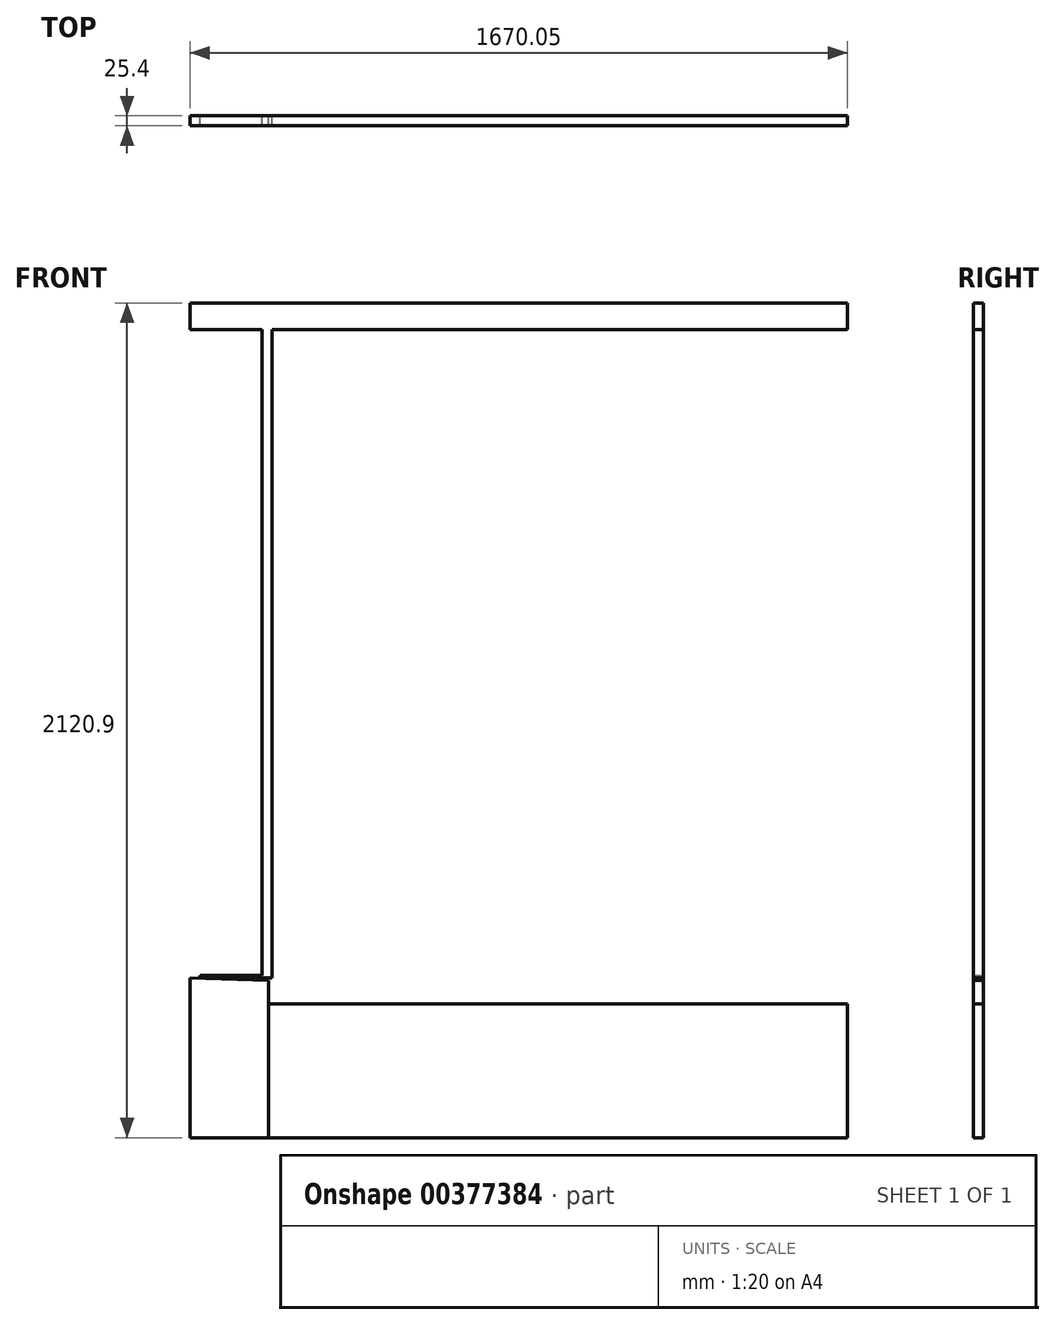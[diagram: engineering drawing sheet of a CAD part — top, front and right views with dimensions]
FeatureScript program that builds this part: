
annotation { "Feature Type Name" : "Feature", "Feature Type Description" : "" }
export const myFeature = defineFeature(function(context is Context, id is Id, definition is map)
    precondition{}
    {
        {
            var Q0;
            Q0=qCreatedBy(makeId("Front.planeOp"),FACE);
            var sketch = newSketch(context, id + "F0", { "sketchPlane" : qUnion([Q0])});
            skLineSegment(sketch, "E0.bottom", {"start": v(2555.45, 68.69) * mm, "end": v(4025.48, 68.69) * mm});
            skLineSegment(sketch, "E0.top", {"start": v(2555.45, 408.41) * mm, "end": v(4025.48, 408.41) * mm});
            skLineSegment(sketch, "E0.left", {"start": v(2555.45, 68.69) * mm, "end": v(2555.45, 408.41) * mm});
            skLineSegment(sketch, "E0.right", {"start": v(4025.48, 68.69) * mm, "end": v(4025.48, 408.41) * mm});
            skLineSegment(sketch, "E1", {"start": v(4025.48, 408.41) * mm, "end": v(4025.48, 2416.76) * mm});
            skLineSegment(sketch, "E2.bottom", {"start": v(4025.48, 2416.76) * mm, "end": v(4078.17, 2416.76) * mm});
            skLineSegment(sketch, "E2.top", {"start": v(4025.48, 68.69) * mm, "end": v(4078.17, 68.69) * mm});
            skLineSegment(sketch, "E2.left", {"start": v(4025.48, 2416.76) * mm, "end": v(4025.48, 68.69) * mm});
            skLineSegment(sketch, "E2.right", {"start": v(4078.17, 2416.76) * mm, "end": v(4078.17, 68.69) * mm});
            skLineSegment(sketch, "E3.bottom", {"start": v(2555.45, 68.69) * mm, "end": v(2355.43, 68.69) * mm});
            skLineSegment(sketch, "E3.left", {"start": v(2555.45, 68.69) * mm, "end": v(2555.45, 468.74) * mm});
            skLineSegment(sketch, "E3.right", {"start": v(2355.43, 68.69) * mm, "end": v(2355.43, 475.09) * mm});
            skLineSegment(sketch, "E4.bottom", {"start": v(2355.43, 68.69) * mm, "end": v(2263.37, 68.69) * mm});
            skLineSegment(sketch, "E4.top", {"start": v(2355.43, 2416.76) * mm, "end": v(2263.37, 2416.76) * mm});
            skLineSegment(sketch, "E4.left", {"start": v(2355.43, 68.69) * mm, "end": v(2355.43, 2416.76) * mm});
            skLineSegment(sketch, "E4.right", {"start": v(2263.37, 68.69) * mm, "end": v(2263.37, 2416.76) * mm});
            skArc(sketch, "E5", {"start": v(4025.48, 1787.6) * mm, "mid": v(3948.24, 1781.25) * mm, "end": v(3899.62, 1720.9) * mm});
            skArc(sketch, "E6.0", {"start": v(4025.48, 1811.72) * mm, "mid": v(3931.19, 1798.13) * mm, "end": v(3875.75, 1720.66) * mm});
            skLineSegment(sketch, "E7.bottom", {"start": v(3929.15, 1720.9) * mm, "end": v(3847.85, 1720.9) * mm});
            skLineSegment(sketch, "E7.top", {"start": v(3929.15, 1699.94) * mm, "end": v(3847.85, 1699.94) * mm});
            skLineSegment(sketch, "E7.left", {"start": v(3929.15, 1720.9) * mm, "end": v(3929.15, 1699.94) * mm});
            skLineSegment(sketch, "E7.right", {"start": v(3847.85, 1720.9) * mm, "end": v(3847.85, 1699.94) * mm});
            skLineSegment(sketch, "E8", {"start": v(2555.45, 468.74) * mm, "end": v(2355.43, 475.09) * mm});
            skLineSegment(sketch, "E9", {"start": v(3290.46, 408.41) * mm, "end": v(3290.46, 2122.26) * mm, "construction": true});
            skLineSegment(sketch, "E10", {"start": v(2355.43, 2122.26) * mm, "end": v(4025.48, 2122.26) * mm});
            skLineSegment(sketch, "E11", {"start": v(2355.43, 2189.59) * mm, "end": v(4025.48, 2189.59) * mm});
            skLineSegment(sketch, "E12.bottom", {"start": v(2355.43, 2122.26) * mm, "end": v(2380.83, 2122.26) * mm});
            skLineSegment(sketch, "E12.top", {"start": v(2355.43, 475.08) * mm, "end": v(2380.83, 475.08) * mm});
            skLineSegment(sketch, "E12.left", {"start": v(2355.43, 2122.26) * mm, "end": v(2355.43, 475.08) * mm});
            skLineSegment(sketch, "E12.right", {"start": v(2380.83, 2122.26) * mm, "end": v(2380.83, 475.08) * mm});
            skLineSegment(sketch, "E13.bottom", {"start": v(2537.99, 475.08) * mm, "end": v(2563.39, 475.08) * mm});
            skLineSegment(sketch, "E13.top", {"start": v(2537.99, 2122.26) * mm, "end": v(2563.39, 2122.26) * mm});
            skLineSegment(sketch, "E13.left", {"start": v(2537.99, 475.08) * mm, "end": v(2537.99, 2122.26) * mm});
            skLineSegment(sketch, "E13.right", {"start": v(2563.39, 475.08) * mm, "end": v(2563.39, 2122.26) * mm});
            skLineSegment(sketch, "E14.bottom", {"start": v(2380.83, 475.08) * mm, "end": v(2537.99, 475.08) * mm});
            skLineSegment(sketch, "E14.top", {"start": v(2380.83, 480.79) * mm, "end": v(2537.99, 480.79) * mm});
            skLineSegment(sketch, "E14.left", {"start": v(2380.83, 475.08) * mm, "end": v(2380.83, 480.79) * mm});
            skLineSegment(sketch, "E14.right", {"start": v(2537.99, 475.08) * mm, "end": v(2537.99, 480.79) * mm});
            skLineSegment(sketch, "E15.bottom", {"start": v(2563.39, 408.41) * mm, "end": v(2587.02, 408.41) * mm});
            skLineSegment(sketch, "E15.top", {"start": v(2563.39, 2122.26) * mm, "end": v(2587.02, 2122.26) * mm});
            skLineSegment(sketch, "E15.left", {"start": v(2563.39, 408.41) * mm, "end": v(2563.39, 2122.26) * mm});
            skLineSegment(sketch, "E15.right", {"start": v(2587.02, 408.41) * mm, "end": v(2587.02, 2122.26) * mm});
            skSolve(sketch);
        }
        {
            var Q0;
            {var subQ4=sQuery(id+"F0.wireOp",EDGE,"E11");Q0=makeQuery(id+"F0.imprint","IMPRINT",FACE,{"disambiguationData":[TD([[makeQuery(id+"F0.imprint","IMPRINT",EDGE,{"derivedFrom":subQ4}),-1.0]])]});}
            var Q1;
            {var subQ3=sQuery(id+"F0.wireOp",EDGE,"E12.bottom");Q1=makeQuery(id+"F0.imprint","IMPRINT",FACE,{"disambiguationData":[TD([[makeQuery(id+"F0.imprint","IMPRINT",EDGE,{"derivedFrom":subQ3}),-1.0]])]});}
            var Q2;
            {var subQ1=sQuery(id+"F0.wireOp",EDGE,"E13.bottom");Q2=makeQuery(id+"F0.imprint","IMPRINT",FACE,{"disambiguationData":[TD([[makeQuery(id+"F0.imprint","IMPRINT",EDGE,{"derivedFrom":subQ1}),1.0]])]});}
            var Q3;
            {var subQ3=sQuery(id+"F0.wireOp",EDGE,"E15.bottom");Q3=makeQuery(id+"F0.imprint","IMPRINT",FACE,{"disambiguationData":[TD([[makeQuery(id+"F0.imprint","IMPRINT",EDGE,{"derivedFrom":subQ3}),1.0]])]});}
            var Q4;
            Q4=makeQuery(id+"F0.imprint","IMPRINT",FACE,{"disambiguationData":[TD([[makeQuery(id+"F0.imprint","IMPRINT",EDGE,{"derivedFrom":sQuery(id+"F0.wireOp",EDGE,"E14.bottom")}),1.0]])]});
            var Q5;
            {var subQ4=sQuery(id+"F0.wireOp",EDGE,"E3.bottom");Q5=makeQuery(id+"F0.imprint","IMPRINT",FACE,{"disambiguationData":[TD([[makeQuery(id+"F0.imprint","IMPRINT",EDGE,{"derivedFrom":subQ4}),-1.0]])]});}
            extrude(context, id + "F1", {"entities" : qUnion([Q0, Q1, Q2, Q3, Q4, Q5]), "depth" : 25.4 * mm});
        }
        {
            var Q0;
            {var subQ5=sQuery(id+"F0.wireOp",EDGE,"E0.bottom");Q0=makeQuery(id+"F0.imprint","IMPRINT",FACE,{"disambiguationData":[TD([[makeQuery(id+"F0.imprint","IMPRINT",EDGE,{"derivedFrom":subQ5}),1.0]])]});}
            extrude(context, id + "F2", {"entities" : qUnion([Q0]), "depth" : 25.4 * mm});
        }
    });
